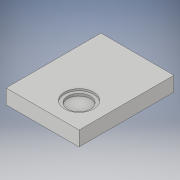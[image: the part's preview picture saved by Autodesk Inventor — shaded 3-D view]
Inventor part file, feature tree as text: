
AUTODESK INVENTOR PART (.ipt)
format: ipt  version: 2017 SP1 (Build 210196100, 196)  size: 220,160 bytes
history: native  units: in
note: dims shown in document units (in); Inventor stores cm internally (conversion verified against a paired STEP export)
features: extrude x3, sketch x3, projected_geometry x1
ambient origin geometry x8: Origin, YZ Plane, XZ Plane, XY Plane, X Axis, Y Axis, Z Axis, Center Point
bodies: Solid1 (feature_tree)
feature tree (7):
  extrude  "Extrusion1"  Depth=6.5in
  extrude  "Extrusion2"  Depth=1.0in
  extrude  "Extrusion3"  Depth=0.155in
  sketch  "Sketch1"  dims[d0=5.0in d1=6.5in]
  sketch  "Sketch2"  dims[d2=1.0in d3=0.0in d4=2.0in]
  projected_geometry  "Projected Loop1"
  sketch  "Sketch3"  dims[d5=1.75in d6=1.75in d7=0.125in d8=0.0in d9=1.56in d10=0.155in d11=0.0in]
